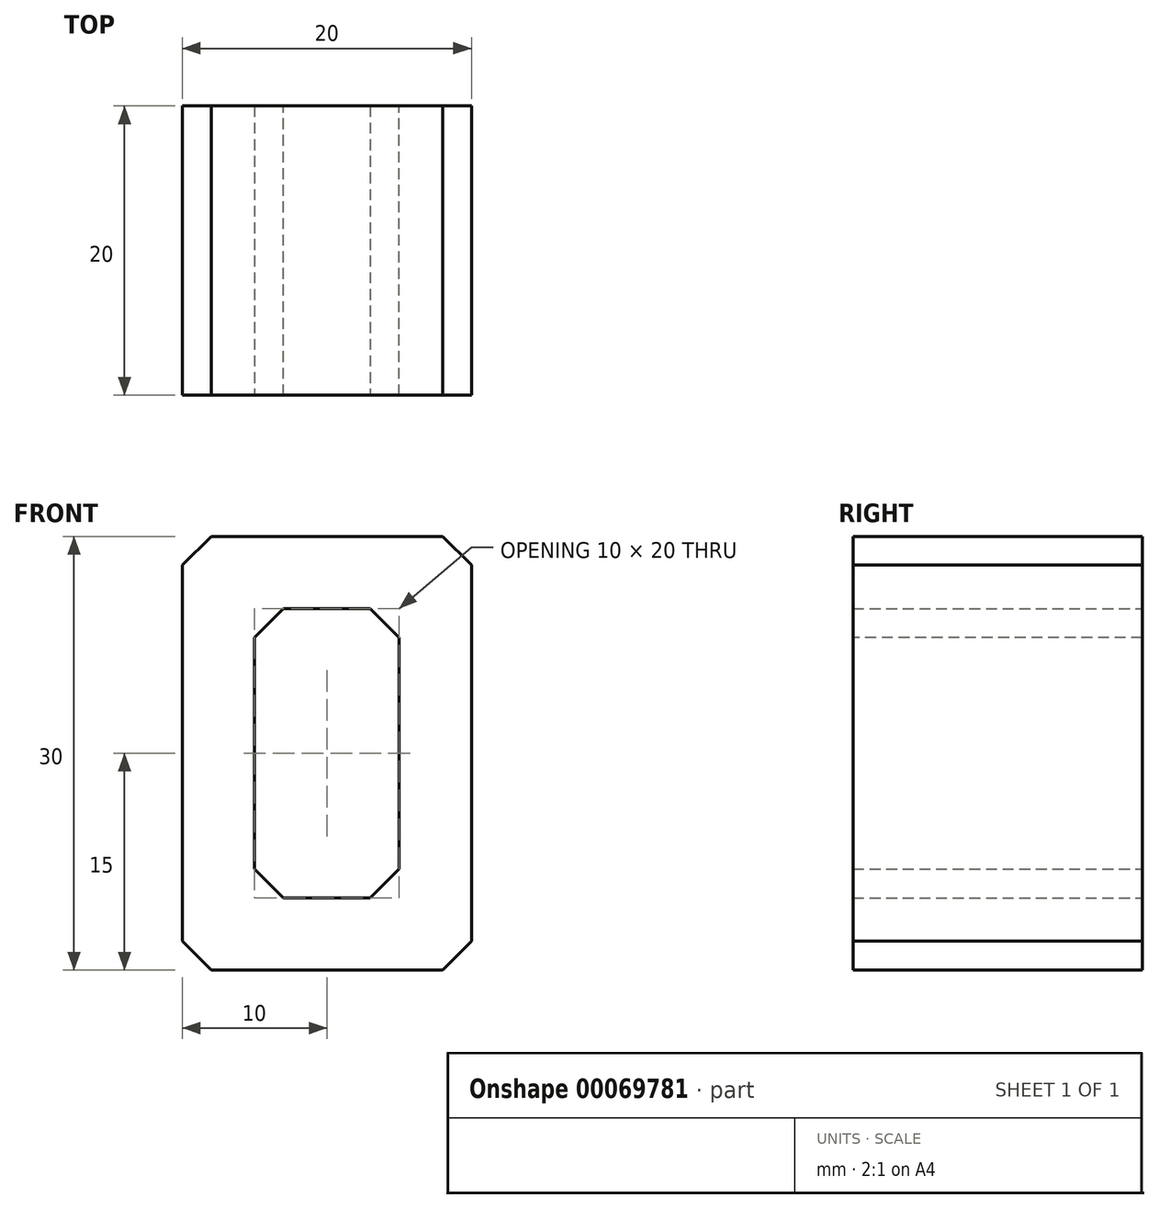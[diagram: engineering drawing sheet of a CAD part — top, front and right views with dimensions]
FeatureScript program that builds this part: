
annotation { "Feature Type Name" : "Feature", "Feature Type Description" : "" }
export const myFeature = defineFeature(function(context is Context, id is Id, definition is map)
    precondition{}
    {
        {
            var Q0;
            Q0=qCreatedBy(makeId("Front.planeOp"),FACE);
            var sketch = newSketch(context, id + "F0", { "sketchPlane" : qUnion([Q0])});
            skLineSegment(sketch, "E0.bottom", {"start": v(0, 0) * mm, "end": v(20, 0) * mm});
            skLineSegment(sketch, "E0.top", {"start": v(0, 30) * mm, "end": v(20, 30) * mm});
            skLineSegment(sketch, "E0.left", {"start": v(0, 0) * mm, "end": v(0, 30) * mm});
            skLineSegment(sketch, "E1", {"start": v(15, 25) * mm, "end": v(5, 25) * mm});
            skLineSegment(sketch, "E2", {"start": v(5, 5) * mm, "end": v(15, 5) * mm});
            skLineSegment(sketch, "E3", {"start": v(5, 25) * mm, "end": v(5, 5) * mm});
            skLineSegment(sketch, "E4", {"start": v(20, 30) * mm, "end": v(20, 0) * mm});
            skLineSegment(sketch, "E5", {"start": v(15, 25) * mm, "end": v(15, 5) * mm});
            skSolve(sketch);
        }
        {
            var Q0;
            Q0=makeQuery(id+"F0.imprint","IMPRINT",FACE,{"disambiguationData":[TD([[makeQuery(id+"F0.imprint","IMPRINT",EDGE,{"derivedFrom":sQuery(id+"F0.wireOp",EDGE,"E0.bottom")}),1.0]])]});
            extrude(context, id + "F1", {"entities" : qUnion([Q0]), "depth" : 20 * mm});
        }
        {
            var Q0;
            Q0=makeQuery(id+"F1.opExtrude","SWEPT_EDGE",EDGE,{"disambiguationData":[OSD([sQuery(id+"F0.wireOp",EDGE,"E0.top"),sQuery(id+"F0.wireOp",EDGE,"546d4a55-b7a7-4c53-8adf-55eec95d67e9.trimOffspring")])]});
            var Q1;
            Q1=makeQuery(id+"F1.opExtrude","SWEPT_EDGE",EDGE,{"disambiguationData":[OSD([sQuery(id+"F0.wireOp",EDGE,"E0.top"),sQuery(id+"F0.wireOp",EDGE,"E0.left")])]});
            var Q2;
            Q2=makeQuery(id+"F1.opExtrude","SWEPT_EDGE",EDGE,{"disambiguationData":[OSD([sQuery(id+"F0.wireOp",EDGE,"E0.bottom"),sQuery(id+"F0.wireOp",EDGE,"E0.right")])]});
            var Q3;
            Q3=makeQuery(id+"F1.opExtrude","SWEPT_EDGE",EDGE,{"disambiguationData":[OSD([sQuery(id+"F0.wireOp",EDGE,"E0.bottom"),sQuery(id+"F0.wireOp",EDGE,"E0.left")])]});
            var Q4;
            Q4=makeQuery(id+"F1.opExtrude","SWEPT_EDGE",EDGE,{"disambiguationData":[OSD([sQuery(id+"F0.wireOp",EDGE,"E1"),sQuery(id+"F0.wireOp",EDGE,"E3")])]});
            var Q5;
            Q5=makeQuery(id+"F1.opExtrude","SWEPT_EDGE",EDGE,{"disambiguationData":[OSD([sQuery(id+"F0.wireOp",EDGE,"E2"),sQuery(id+"F0.wireOp",EDGE,"E3")])]});
            var Q6;
            Q6=makeQuery(id+"F1.opExtrude","SWEPT_EDGE",EDGE,{"disambiguationData":[OSD([sQuery(id+"F0.wireOp",EDGE,"E1"),sQuery(id+"F0.wireOp",EDGE,"n1ijJ5YP-M1Tn-JsJj-iDBB-TBpcYrNwhwjC")])]});
            var Q7;
            Q7=makeQuery(id+"F1.opExtrude","SWEPT_EDGE",EDGE,{"disambiguationData":[OSD([sQuery(id+"F0.wireOp",EDGE,"E2"),sQuery(id+"F0.wireOp",EDGE,"918f8cf8-ef64-43a8-bcf4-1f458dc78bbe.trimOffspring")])]});
            chamfer(context, id + "F2", {"entities" : qUnion([Q0, Q1, Q2, Q3, Q4, Q5, Q6, Q7]), "width" : 2 * mm, "tangentPropagation" : true});
        }
    });
